# Revit family: Deca_Cuba de cozinha_Dream_CC.630.50.STD
name_source: partatom
category: Plumbing Fixtures
units: mm (PartAtom-declared; Revit-internal decimal feet)

## family parameters
Cut with Voids When Loaded = No
Host = Face
Part Type = Normal
Room Calculation Point = No
Round Connector Dimension = Use Radius
Shared = No

## types (2) — shared parameters
Acompanha o Produto = Acompanha Bisnaga de Silicone; parafuso, grampo e suporte para fixação; Kit Sifão e Valvula de Escoamento e válvula escoamento com mangueira do ladrão
Aprovado por = quattroD
Atendimento ao Cliente = 0800-0117073
Categoria = CUBAS COZINHA
Composição Anel Vedação = -
Composição Assento = -
Composição Básica = Aço Inoxidável
Composição Componente = -
Consumo = -
Cor Interna = -
Cor Secundária = -
Cores Componente = -
Criado por = quattroD
Código Pai = CC.630.50.STD
Description = Cuba de cozinha
Diâmetro Ponto de Esgoto = 25 mm  [stored 0.082021 ft]
Informações Complementares = -
Itens de Instalação = -
Linha = Cubas de Cozinha
Manufacturer = Deca
Norma = Não Possui
Peso Líquido (Kg) = 4.8
Pressão máx. funcionamento = -
Pressão mín. Aquec. Acúmulo = -
Pressão mín. Aquec. Passagem = -
Pressão mín. funcionamento = -
Raio Ponto de Esgoto = 13 mm  [stored 0.0426509 ft]
Saída de Esgoto = -
Segmento = Cozinha Luxo
Tipo de dispositivo economizador = -
Tipo de mecanismo utilizado = -
Tipo de rosca de entrada = -
Tipo de rosca de saída = -
URL = www.deca.com.br
Vazão na Pressão máx. (L/min) = -
Vazão na Pressão mín. (L/min) = -
zero-valued in all types: Default Elevation

## per-type parameters (varying)
| type | Cor Principal | Material | Model |
| CC.630.50.STD.CU_Cobre | Cobre | Deca_Cobre | CC.630.50.STD.CU |
| CC.630.50.STD.SN_Estanho | Estanho | Deca_Estanho | CC.630.50.STD.SN |

note: [stored X ft] marks values corroborated as IEEE doubles in the binary element streams (Revit-internal decimal feet)

## geometry (parser evidence)
native form markers: Sweep x2
no freeform markers — native parametric forms only
